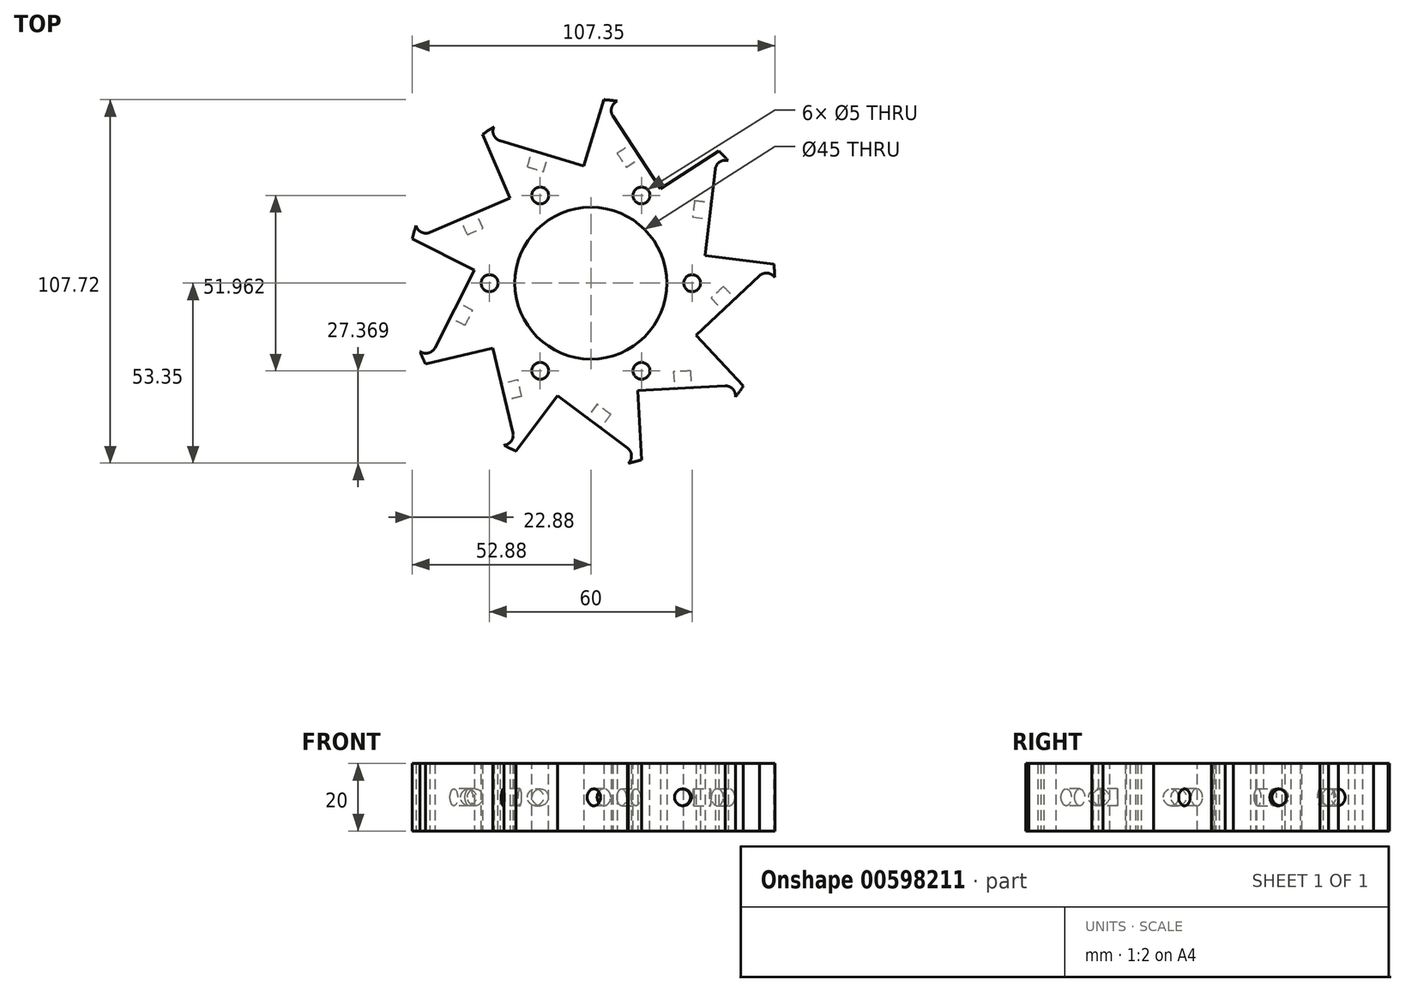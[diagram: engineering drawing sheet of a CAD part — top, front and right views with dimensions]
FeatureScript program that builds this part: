
annotation { "Feature Type Name" : "Feature", "Feature Type Description" : "" }
export const myFeature = defineFeature(function(context is Context, id is Id, definition is map)
    precondition{}
    {
        {
            var Q0;
            Q0=qCreatedBy(makeId("Top.planeOp"),FACE);
            var sketch = newSketch(context, id + "F0", { "sketchPlane" : qUnion([Q0])});
            skCircle(sketch, "E0", {"center": v(0, 0) * mm, "radius": 54.5 * mm});
            skPoint(sketch, "E1.end.orphan", {"position": v(37.16, -28.22) * mm});
            skPoint(sketch, "E2.orphan", {"position": v(26.14, -22.13) * mm});
            skCircle(sketch, "E3", {"center": v(0, 0) * mm, "radius": 22.5 * mm});
            skArc(sketch, "E4", {"start": v(54.47, 1.7) * mm, "mid": v(52.36, 2.98) * mm, "end": v(50, 2.24) * mm});
            skLineSegment(sketch, "E5", {"start": v(31.12, -15.5) * mm, "end": v(50, 2.24) * mm});
            skLineSegment(sketch, "E6", {"start": v(31.12, -15.5) * mm, "end": v(45.19, -30.47) * mm});
            skLineSegment(sketch, "E7.1.0", {"start": v(33.8, 8.14) * mm, "end": v(36.86, 33.85) * mm});
            skArc(sketch, "E7.1.1", {"start": v(40.64, 36.32) * mm, "mid": v(38.2, 35.94) * mm, "end": v(36.86, 33.85) * mm});
            skLineSegment(sketch, "E7.1.2", {"start": v(33.8, 8.14) * mm, "end": v(54.2, 5.7) * mm});
            skLineSegment(sketch, "E7.2.0", {"start": v(20.66, 27.96) * mm, "end": v(6.48, 49.63) * mm});
            skArc(sketch, "E7.2.1", {"start": v(7.79, 53.94) * mm, "mid": v(6.16, 52.08) * mm, "end": v(6.48, 49.63) * mm});
            skLineSegment(sketch, "E7.2.2", {"start": v(20.66, 27.96) * mm, "end": v(37.85, 39.2) * mm});
            skLineSegment(sketch, "E7.3.0", {"start": v(-2.14, 34.7) * mm, "end": v(-26.94, 42.18) * mm});
            skArc(sketch, "E7.3.1", {"start": v(-28.7, 46.33) * mm, "mid": v(-28.76, 43.85) * mm, "end": v(-26.94, 42.18) * mm});
            skLineSegment(sketch, "E7.3.2", {"start": v(-2.14, 34.7) * mm, "end": v(3.8, 54.37) * mm});
            skLineSegment(sketch, "E7.4.0", {"start": v(-23.94, 25.2) * mm, "end": v(-47.75, 15) * mm});
            skArc(sketch, "E7.4.1", {"start": v(-51.77, 17.04) * mm, "mid": v(-50.22, 15.1) * mm, "end": v(-47.75, 15) * mm});
            skLineSegment(sketch, "E7.4.2", {"start": v(-23.94, 25.2) * mm, "end": v(-32.04, 44.09) * mm});
            skLineSegment(sketch, "E7.5.0", {"start": v(-34.54, 3.91) * mm, "end": v(-46.22, -19.2) * mm});
            skArc(sketch, "E7.5.1", {"start": v(-50.6, -20.23) * mm, "mid": v(-48.18, -20.7) * mm, "end": v(-46.22, -19.2) * mm});
            skLineSegment(sketch, "E7.5.2", {"start": v(-34.54, 3.91) * mm, "end": v(-52.88, 13.18) * mm});
            skLineSegment(sketch, "E7.6.0", {"start": v(-28.98, -19.2) * mm, "end": v(-23.06, -44.42) * mm});
            skArc(sketch, "E7.6.1", {"start": v(-25.77, -48.02) * mm, "mid": v(-23.6, -46.83) * mm, "end": v(-23.06, -44.42) * mm});
            skLineSegment(sketch, "E7.6.2", {"start": v(-28.98, -19.2) * mm, "end": v(-48.98, -23.9) * mm});
            skLineSegment(sketch, "E7.7.0", {"start": v(-9.85, -33.34) * mm, "end": v(10.88, -48.85) * mm});
            skArc(sketch, "E7.7.1", {"start": v(11.13, -53.35) * mm, "mid": v(12.03, -51.05) * mm, "end": v(10.88, -48.85) * mm});
            skLineSegment(sketch, "E7.7.2", {"start": v(-9.85, -33.34) * mm, "end": v(-22.16, -49.8) * mm});
            skLineSegment(sketch, "E7.8.0", {"start": v(13.88, -31.87) * mm, "end": v(39.74, -30.43) * mm});
            skArc(sketch, "E7.8.1", {"start": v(42.82, -33.71) * mm, "mid": v(42.02, -31.37) * mm, "end": v(39.74, -30.43) * mm});
            skLineSegment(sketch, "E7.8.2", {"start": v(13.88, -31.87) * mm, "end": v(15.03, -52.39) * mm});
            skSolve(sketch);
        }
        {
            var Q0;
            {var subQ15=sQuery(id+"F0.wireOp",EDGE,"8e3Yusj1-4p0S-ZVll-QxbA-hZj1eCrwd1Jn");Q0=makeQuery(id+"F0.imprint","IMPRINT",FACE,{"disambiguationData":[TD([[makeQuery(id+"F0.imprint","IMPRINT",EDGE,{"derivedFrom":subQ15}),-1.0]])]});}
            var Q1;
            Q1=makeQuery(id+"F0.imprint","IMPRINT",FACE,{"disambiguationData":[TD([[makeQuery(id+"F0.imprint","IMPRINT",EDGE,{"derivedFrom":sQuery(id+"F0.wireOp",EDGE,"E3")}),-1.0]])]});
            extrude(context, id + "F1", {"entities" : qUnion([Q0, Q1]), "depth" : 20 * mm, "offsetDistance" : 25 * mm});
        }
        {
            var Q0;
            Q0=makeQuery(id+"F1.opExtrude","CAP_FACE",FACE,{"disambiguationData":[OSD([sQuery(id+"F0.wireOp",EDGE,"E0"),sQuery(id+"F0.wireOp",EDGE,"pzBCD7Al-y2ax-SI5w-KrCM-7ZoreVbjkYuo"),sQuery(id+"F0.wireOp",EDGE,"8e3Yusj1-4p0S-ZVll-QxbA-hZj1eCrwd1Jn"),sQuery(id+"F0.wireOp",EDGE,"tBLSvFii-JbDE-6F1s-xYhB-tNo5b2TwvyA9"),sQuery(id+"F0.wireOp",EDGE,"EvnPPQOH-lV2L-kl6y-B8St-3MgRml6kQuEM"),sQuery(id+"F0.wireOp",EDGE,"2a86d717-9e81-4316-b34b-3857465c11ef.1.0"),sQuery(id+"F0.wireOp",EDGE,"2a86d717-9e81-4316-b34b-3857465c11ef.1.1"),sQuery(id+"F0.wireOp",EDGE,"2a86d717-9e81-4316-b34b-3857465c11ef.1.2"),sQuery(id+"F0.wireOp",EDGE,"2a86d717-9e81-4316-b34b-3857465c11ef.1.3"),sQuery(id+"F0.wireOp",EDGE,"2a86d717-9e81-4316-b34b-3857465c11ef.2.0"),sQuery(id+"F0.wireOp",EDGE,"2a86d717-9e81-4316-b34b-3857465c11ef.2.1"),sQuery(id+"F0.wireOp",EDGE,"2a86d717-9e81-4316-b34b-3857465c11ef.2.2"),sQuery(id+"F0.wireOp",EDGE,"2a86d717-9e81-4316-b34b-3857465c11ef.2.3"),sQuery(id+"F0.wireOp",EDGE,"2a86d717-9e81-4316-b34b-3857465c11ef.3.0"),sQuery(id+"F0.wireOp",EDGE,"2a86d717-9e81-4316-b34b-3857465c11ef.3.1"),sQuery(id+"F0.wireOp",EDGE,"2a86d717-9e81-4316-b34b-3857465c11ef.3.2"),sQuery(id+"F0.wireOp",EDGE,"2a86d717-9e81-4316-b34b-3857465c11ef.3.3"),sQuery(id+"F0.wireOp",EDGE,"2a86d717-9e81-4316-b34b-3857465c11ef.4.0"),sQuery(id+"F0.wireOp",EDGE,"2a86d717-9e81-4316-b34b-3857465c11ef.4.1"),sQuery(id+"F0.wireOp",EDGE,"2a86d717-9e81-4316-b34b-3857465c11ef.4.2"),sQuery(id+"F0.wireOp",EDGE,"2a86d717-9e81-4316-b34b-3857465c11ef.4.3"),sQuery(id+"F0.wireOp",EDGE,"2a86d717-9e81-4316-b34b-3857465c11ef.5.0"),sQuery(id+"F0.wireOp",EDGE,"2a86d717-9e81-4316-b34b-3857465c11ef.5.1"),sQuery(id+"F0.wireOp",EDGE,"2a86d717-9e81-4316-b34b-3857465c11ef.5.2"),sQuery(id+"F0.wireOp",EDGE,"2a86d717-9e81-4316-b34b-3857465c11ef.5.3"),sQuery(id+"F0.wireOp",EDGE,"2a86d717-9e81-4316-b34b-3857465c11ef.6.0"),sQuery(id+"F0.wireOp",EDGE,"2a86d717-9e81-4316-b34b-3857465c11ef.6.1"),sQuery(id+"F0.wireOp",EDGE,"2a86d717-9e81-4316-b34b-3857465c11ef.6.2"),sQuery(id+"F0.wireOp",EDGE,"2a86d717-9e81-4316-b34b-3857465c11ef.6.3"),sQuery(id+"F0.wireOp",EDGE,"E3")])],"isStart":false});
            var sketch = newSketch(context, id + "F2", { "sketchPlane" : qUnion([Q0])});
            skLineSegment(sketch, "E8", {"start": v(0, 0) * mm, "end": v(30, 0) * mm});
            skCircle(sketch, "E9", {"center": v(30, 0) * mm, "radius": 2.5 * mm});
            skCircle(sketch, "E10.1.0", {"center": v(15, 25.98) * mm, "radius": 2.5 * mm});
            skCircle(sketch, "E10.2.0", {"center": v(-15, 25.98) * mm, "radius": 2.5 * mm});
            skCircle(sketch, "E10.3.0", {"center": v(-30, 0) * mm, "radius": 2.5 * mm});
            skCircle(sketch, "E10.4.0", {"center": v(-15, -25.98) * mm, "radius": 2.5 * mm});
            skCircle(sketch, "E10.5.0", {"center": v(15, -25.98) * mm, "radius": 2.5 * mm});
            skPoint(sketch, "E10.center", {"position": v(0, 0) * mm});
            skSolve(sketch);
        }
        {
            var Q0;
            Q0=makeQuery(id+"F2.imprint","IMPRINT",FACE,{"disambiguationData":[TD([[makeQuery(id+"F2.imprint","IMPRINT",EDGE,{"derivedFrom":sQuery(id+"F2.wireOp",EDGE,"E10.1.0")}),1.0]])]});
            var Q1;
            Q1=makeQuery(id+"F2.imprint","IMPRINT",FACE,{"disambiguationData":[TD([[makeQuery(id+"F2.imprint","IMPRINT",EDGE,{"derivedFrom":sQuery(id+"F2.wireOp",EDGE,"E9")}),1.0]])]});
            var Q2;
            Q2=makeQuery(id+"F2.imprint","IMPRINT",FACE,{"disambiguationData":[TD([[makeQuery(id+"F2.imprint","IMPRINT",EDGE,{"derivedFrom":sQuery(id+"F2.wireOp",EDGE,"E10.5.0")}),1.0]])]});
            var Q3;
            Q3=makeQuery(id+"F2.imprint","IMPRINT",FACE,{"disambiguationData":[TD([[makeQuery(id+"F2.imprint","IMPRINT",EDGE,{"derivedFrom":sQuery(id+"F2.wireOp",EDGE,"E10.4.0")}),1.0]])]});
            var Q4;
            Q4=makeQuery(id+"F2.imprint","IMPRINT",FACE,{"disambiguationData":[TD([[makeQuery(id+"F2.imprint","IMPRINT",EDGE,{"derivedFrom":sQuery(id+"F2.wireOp",EDGE,"E10.3.0")}),1.0]])]});
            var Q5;
            Q5=makeQuery(id+"F2.imprint","IMPRINT",FACE,{"disambiguationData":[TD([[makeQuery(id+"F2.imprint","IMPRINT",EDGE,{"derivedFrom":sQuery(id+"F2.wireOp",EDGE,"E10.2.0")}),1.0]])]});
            extrude(context, id + "F3", {"entities" : qUnion([Q0, Q1, Q2, Q3, Q4, Q5]), "operationType" : NewBodyOperationType.REMOVE, "endBound" : BoundingType.THROUGH_ALL, "oppositeDirection" : true, "depth" : 25 * mm, "offsetDistance" : 25 * mm});
        }
        {
            var Q0;
            Q0=makeQuery(id+"F1.opExtrude","SWEPT_FACE",FACE,{"disambiguationData":[OSD([sQuery(id+"F0.wireOp",EDGE,"E7.1.0")])]});
            var sketch = newSketch(context, id + "F4", { "sketchPlane" : qUnion([Q0])});
            skCircle(sketch, "E11", {"center": v(25.48, 10) * mm, "radius": 2.5 * mm});
            skSolve(sketch);
        }
        {
            var Q0;
            Q0=makeQuery(id+"F4.imprint","IMPRINT",FACE,{"disambiguationData":[TD([[makeQuery(id+"F4.imprint","IMPRINT",EDGE,{"derivedFrom":sQuery(id+"F4.wireOp",EDGE,"E11")}),1.0]])]});
            extrude(context, id + "F5", {"entities" : qUnion([Q0]), "operationType" : NewBodyOperationType.REMOVE, "oppositeDirection" : true, "depth" : 5 * mm, "offsetDistance" : 25 * mm});
        }
        {
            var Q0;
            Q0=makeQuery(id+"F1.opExtrude","SWEPT_FACE",FACE,{"disambiguationData":[OSD([sQuery(id+"F0.wireOp",EDGE,"E7.2.0")])]});
            var sketch = newSketch(context, id + "F6", { "sketchPlane" : qUnion([Q0])});
            skPoint(sketch, "E12.endSnap0", {"position": v(37.98, 10) * mm});
            skPoint(sketch, "E13.orphan", {"position": v(17.82, 10) * mm});
            skPoint(sketch, "E14.end.orphan", {"position": v(25.48, 32.54) * mm});
            skPoint(sketch, "E14.start.orphan", {"position": v(37.98, 32.54) * mm});
            skCircle(sketch, "E15", {"center": v(25.48, 10) * mm, "radius": 2.5 * mm});
            skSolve(sketch);
        }
        {
            var Q0;
            Q0=makeQuery(id+"F6.imprint","IMPRINT",FACE,{"disambiguationData":[TD([[makeQuery(id+"F6.imprint","IMPRINT",EDGE,{"derivedFrom":sQuery(id+"F6.wireOp",EDGE,"E15")}),1.0]])]});
            extrude(context, id + "F7", {"entities" : qUnion([Q0]), "operationType" : NewBodyOperationType.REMOVE, "oppositeDirection" : true, "depth" : 5 * mm, "offsetDistance" : 25 * mm});
        }
        {
            var Q0;
            Q0=makeQuery(id+"F1.opExtrude","SWEPT_FACE",FACE,{"disambiguationData":[OSD([sQuery(id+"F0.wireOp",EDGE,"E7.3.0")])]});
            var sketch = newSketch(context, id + "F8", { "sketchPlane" : qUnion([Q0])});
            skCircle(sketch, "E16", {"center": v(25.48, 10) * mm, "radius": 2.5 * mm});
            skSolve(sketch);
        }
        {
            var Q0;
            Q0=makeQuery(id+"F8.imprint","IMPRINT",FACE,{"disambiguationData":[TD([[makeQuery(id+"F8.imprint","IMPRINT",EDGE,{"derivedFrom":sQuery(id+"F8.wireOp",EDGE,"E16")}),1.0]])]});
            extrude(context, id + "F9", {"entities" : qUnion([Q0]), "operationType" : NewBodyOperationType.REMOVE, "oppositeDirection" : true, "depth" : 5 * mm, "offsetDistance" : 25 * mm});
        }
        {
            var Q0;
            Q0=makeQuery(id+"F1.opExtrude","SWEPT_FACE",FACE,{"disambiguationData":[OSD([sQuery(id+"F0.wireOp",EDGE,"E7.4.0")])]});
            var sketch = newSketch(context, id + "F10", { "sketchPlane" : qUnion([Q0])});
            skPoint(sketch, "E17.endSnap0", {"position": v(37.98, 10) * mm});
            skPoint(sketch, "E18.orphan", {"position": v(18.7, 10) * mm});
            skPoint(sketch, "E19.end.orphan", {"position": v(25.48, -10.98) * mm});
            skPoint(sketch, "E20.end.orphan", {"position": v(37.98, -10.98) * mm});
            skCircle(sketch, "E21", {"center": v(25.48, 10) * mm, "radius": 2.5 * mm});
            skSolve(sketch);
        }
        {
            var Q0;
            Q0=makeQuery(id+"F10.imprint","IMPRINT",FACE,{"disambiguationData":[TD([[makeQuery(id+"F10.imprint","IMPRINT",EDGE,{"derivedFrom":sQuery(id+"F10.wireOp",EDGE,"E21")}),1.0]])]});
            extrude(context, id + "F11", {"entities" : qUnion([Q0]), "operationType" : NewBodyOperationType.REMOVE, "oppositeDirection" : true, "depth" : 5 * mm, "offsetDistance" : 25 * mm});
        }
        {
            var Q0;
            Q0=makeQuery(id+"F1.opExtrude","SWEPT_FACE",FACE,{"disambiguationData":[OSD([sQuery(id+"F0.wireOp",EDGE,"E7.5.0")])]});
            var sketch = newSketch(context, id + "F12", { "sketchPlane" : qUnion([Q0])});
            skCircle(sketch, "E22", {"center": v(25.48, 10) * mm, "radius": 2.5 * mm});
            skSolve(sketch);
        }
        {
            var Q0;
            Q0=makeQuery(id+"F12.imprint","IMPRINT",FACE,{"disambiguationData":[TD([[makeQuery(id+"F12.imprint","IMPRINT",EDGE,{"derivedFrom":sQuery(id+"F12.wireOp",EDGE,"E22")}),1.0]])]});
            extrude(context, id + "F13", {"entities" : qUnion([Q0]), "operationType" : NewBodyOperationType.REMOVE, "oppositeDirection" : true, "depth" : 5 * mm, "offsetDistance" : 25 * mm});
        }
        {
            var Q0;
            Q0=makeQuery(id+"F1.opExtrude","SWEPT_FACE",FACE,{"disambiguationData":[OSD([sQuery(id+"F0.wireOp",EDGE,"E7.6.0")])]});
            var sketch = newSketch(context, id + "F14", { "sketchPlane" : qUnion([Q0])});
            skCircle(sketch, "E23", {"center": v(25.48, 10) * mm, "radius": 2.5 * mm});
            skSolve(sketch);
        }
        {
            var Q0;
            Q0=makeQuery(id+"F14.imprint","IMPRINT",FACE,{"disambiguationData":[TD([[makeQuery(id+"F14.imprint","IMPRINT",EDGE,{"derivedFrom":sQuery(id+"F14.wireOp",EDGE,"E23")}),1.0]])]});
            extrude(context, id + "F15", {"entities" : qUnion([Q0]), "operationType" : NewBodyOperationType.REMOVE, "oppositeDirection" : true, "depth" : 5 * mm, "offsetDistance" : 25 * mm});
        }
        {
            var Q0;
            Q0=makeQuery(id+"F1.opExtrude","SWEPT_FACE",FACE,{"disambiguationData":[OSD([sQuery(id+"F0.wireOp",EDGE,"E7.7.0")])]});
            var sketch = newSketch(context, id + "F16", { "sketchPlane" : qUnion([Q0])});
            skCircle(sketch, "E24", {"center": v(25.48, 10) * mm, "radius": 2.5 * mm});
            skSolve(sketch);
        }
        {
            var Q0;
            Q0=makeQuery(id+"F16.imprint","IMPRINT",FACE,{"disambiguationData":[TD([[makeQuery(id+"F16.imprint","IMPRINT",EDGE,{"derivedFrom":sQuery(id+"F16.wireOp",EDGE,"E24")}),1.0]])]});
            extrude(context, id + "F17", {"entities" : qUnion([Q0]), "operationType" : NewBodyOperationType.REMOVE, "oppositeDirection" : true, "depth" : 5 * mm, "offsetDistance" : 25 * mm});
        }
        {
            var Q0;
            Q0=makeQuery(id+"F1.opExtrude","SWEPT_FACE",FACE,{"disambiguationData":[OSD([sQuery(id+"F0.wireOp",EDGE,"E7.8.0")])]});
            var sketch = newSketch(context, id + "F18", { "sketchPlane" : qUnion([Q0])});
            skCircle(sketch, "E25", {"center": v(25.48, 10) * mm, "radius": 2.5 * mm});
            skSolve(sketch);
        }
        {
            var Q0;
            Q0=makeQuery(id+"F18.imprint","IMPRINT",FACE,{"disambiguationData":[TD([[makeQuery(id+"F18.imprint","IMPRINT",EDGE,{"derivedFrom":sQuery(id+"F18.wireOp",EDGE,"E25")}),1.0]])]});
            extrude(context, id + "F19", {"entities" : qUnion([Q0]), "operationType" : NewBodyOperationType.REMOVE, "oppositeDirection" : true, "depth" : 5 * mm, "offsetDistance" : 25 * mm});
        }
        {
            var Q0;
            Q0=makeQuery(id+"F1.opExtrude","SWEPT_FACE",FACE,{"disambiguationData":[OSD([sQuery(id+"F0.wireOp",EDGE,"E5")])]});
            var sketch = newSketch(context, id + "F20", { "sketchPlane" : qUnion([Q0])});
            skCircle(sketch, "E26", {"center": v(25.48, 10) * mm, "radius": 2.5 * mm});
            skSolve(sketch);
        }
        {
            var Q0;
            Q0=makeQuery(id+"F20.imprint","IMPRINT",FACE,{"disambiguationData":[TD([[makeQuery(id+"F20.imprint","IMPRINT",EDGE,{"derivedFrom":sQuery(id+"F20.wireOp",EDGE,"E26")}),1.0]])]});
            extrude(context, id + "F21", {"entities" : qUnion([Q0]), "operationType" : NewBodyOperationType.REMOVE, "oppositeDirection" : true, "depth" : 5 * mm, "offsetDistance" : 25 * mm});
        }
    });
